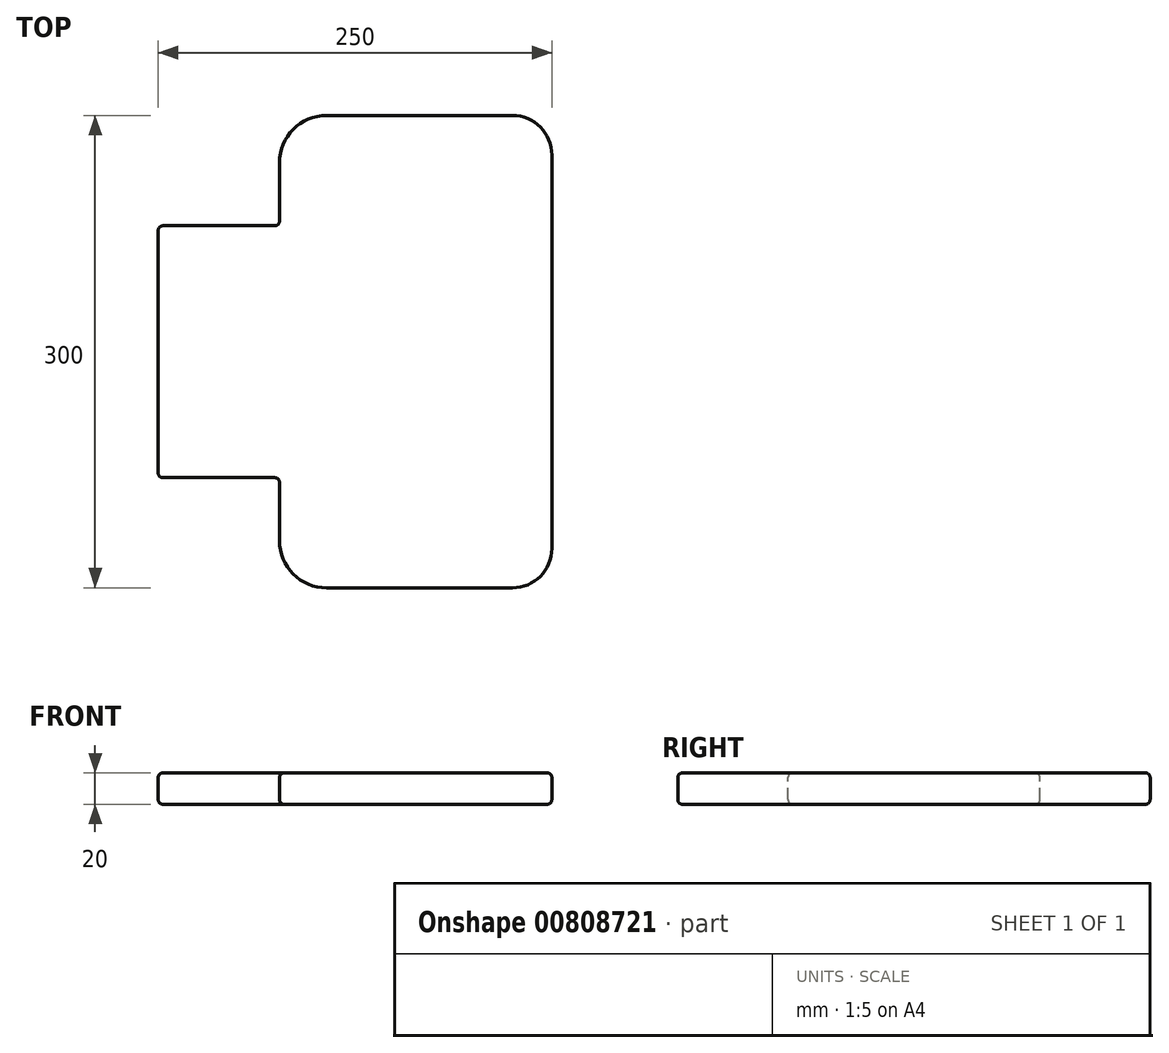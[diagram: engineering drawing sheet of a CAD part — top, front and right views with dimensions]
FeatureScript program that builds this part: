
annotation { "Feature Type Name" : "Feature", "Feature Type Description" : "" }
export const myFeature = defineFeature(function(context is Context, id is Id, definition is map)
    precondition{}
    {
        {
            var Q0;
            Q0=qCreatedBy(makeId("Top.planeOp"),FACE);
            var sketch = newSketch(context, id + "F0", { "sketchPlane" : qUnion([Q0])});
            skLineSegment(sketch, "E0.bottom", {"start": v(100, -150) * mm, "end": v(-100, -150) * mm});
            skLineSegment(sketch, "E0.top", {"start": v(100, 150) * mm, "end": v(-100, 150) * mm});
            skLineSegment(sketch, "E0.left", {"start": v(125, -125) * mm, "end": v(125, 125) * mm});
            skLineSegment(sketch, "E0.right", {"start": v(-125, -125) * mm, "end": v(-125, 125) * mm});
            skPoint(sketch, "E0.middle", {"position": v(0, 0) * mm});
            skPoint(sketch, "E1.visualSharp", {"position": v(-125, 150) * mm});
            skArc(sketch, "E1.filletArc", {"start": v(-100, 150) * mm, "mid": v(-117.68, 142.68) * mm, "end": v(-125, 125) * mm});
            skPoint(sketch, "E2.visualSharp", {"position": v(125, 150) * mm});
            skArc(sketch, "E2.filletArc", {"start": v(125, 125) * mm, "mid": v(117.68, 142.68) * mm, "end": v(100, 150) * mm});
            skPoint(sketch, "E3.visualSharp", {"position": v(125, -150) * mm});
            skArc(sketch, "E3.filletArc", {"start": v(100, -150) * mm, "mid": v(117.68, -142.68) * mm, "end": v(125, -125) * mm});
            skPoint(sketch, "E4.visualSharp", {"position": v(-125, -150) * mm});
            skArc(sketch, "E4.filletArc", {"start": v(-125, -125) * mm, "mid": v(-117.68, -142.68) * mm, "end": v(-100, -150) * mm});
            skSolve(sketch);
        }
        {
            var Q0;
            Q0=makeQuery(id+"F0.imprint","IMPRINT",FACE,{"disambiguationData":[TD([[makeQuery(id+"F0.imprint","IMPRINT",EDGE,{"derivedFrom":sQuery(id+"F0.wireOp",EDGE,"E0.bottom")}),-1.0]])]});
            extrude(context, id + "F1", {"entities" : qUnion([Q0]), "depth" : 20 * mm, "offsetDistance" : 25 * mm});
        }
        {
            var Q0;
            Q0=makeQuery(id+"F1.opExtrude","CAP_FACE",FACE,{"disambiguationData":[OSD([sQuery(id+"F0.wireOp",EDGE,"E0.bottom"),sQuery(id+"F0.wireOp",EDGE,"E0.top"),sQuery(id+"F0.wireOp",EDGE,"E0.left"),sQuery(id+"F0.wireOp",EDGE,"E0.right"),sQuery(id+"F0.wireOp",EDGE,"E1.filletArc"),sQuery(id+"F0.wireOp",EDGE,"E2.filletArc"),sQuery(id+"F0.wireOp",EDGE,"E3.filletArc"),sQuery(id+"F0.wireOp",EDGE,"E4.filletArc")])],"isStart":false});
            var sketch = newSketch(context, id + "F2", { "sketchPlane" : qUnion([Q0])});
            skLineSegment(sketch, "E5.bottom", {"start": v(-146.1, -80) * mm, "end": v(-48, -80) * mm});
            skLineSegment(sketch, "E5.top", {"start": v(-146.1, -176.23) * mm, "end": v(-48, -176.23) * mm});
            skLineSegment(sketch, "E5.left", {"start": v(-146.1, -80) * mm, "end": v(-146.1, -176.23) * mm});
            skLineSegment(sketch, "E5.right", {"start": v(-48, -80) * mm, "end": v(-48, -176.23) * mm});
            skLineSegment(sketch, "E6.MirrorCS", {"start": v(-146.1, 80) * mm, "end": v(-48, 80) * mm});
            skLineSegment(sketch, "E7.MirrorCS", {"start": v(-48, 80) * mm, "end": v(-48, 176.23) * mm});
            skLineSegment(sketch, "E8.MirrorCS", {"start": v(-146.1, 80) * mm, "end": v(-146.1, 176.23) * mm});
            skLineSegment(sketch, "E9.MirrorCS", {"start": v(-146.1, 176.23) * mm, "end": v(-48, 176.23) * mm});
            skSolve(sketch);
        }
        {
            var Q0;
            {var subQ0=makeQuery(id+"F1.opExtrude","CAP_EDGE",EDGE,{"disambiguationData":[OSD([sQuery(id+"F0.wireOp",EDGE,"E4.filletArc")])],"isStart":false});Q0=makeQuery(id+"F2.imprint","IMPRINT",FACE,{"disambiguationData":[TD([[makeQuery(id+"F2.imprint","IMPRINT",EDGE,{"derivedFrom":subQ0}),1.0]])]});}
            var Q1;
            {var subQ1=sQuery(id+"F2.wireOp",EDGE,"E5.top");Q1=makeQuery(id+"F2.imprint","IMPRINT",FACE,{"disambiguationData":[TD([[makeQuery(id+"F2.imprint","IMPRINT",EDGE,{"derivedFrom":subQ1}),1.0]])]});}
            var Q2;
            {var subQ0=sQuery(id+"F2.wireOp",EDGE,"E8.MirrorCS");Q2=makeQuery(id+"F2.imprint","IMPRINT",FACE,{"disambiguationData":[TD([[makeQuery(id+"F2.imprint","IMPRINT",EDGE,{"derivedFrom":subQ0}),-1.0]])]});}
            var Q3;
            {var subQ0=makeQuery(id+"F1.opExtrude","CAP_EDGE",EDGE,{"disambiguationData":[OSD([sQuery(id+"F0.wireOp",EDGE,"E1.filletArc")])],"isStart":false});Q3=makeQuery(id+"F2.imprint","IMPRINT",FACE,{"disambiguationData":[TD([[makeQuery(id+"F2.imprint","IMPRINT",EDGE,{"derivedFrom":subQ0}),1.0]])]});}
            extrude(context, id + "F3", {"entities" : qUnion([Q0, Q1, Q2, Q3]), "operationType" : NewBodyOperationType.REMOVE, "oppositeDirection" : true, "depth" : 25 * mm, "offsetDistance" : 25 * mm});
        }
        {
            var Q0;
            Q0=makeQuery(id+"F3.boolean.opBoolean","INTERSECT",EDGE,{"derivedFrom":[makeQuery(id+"F1.opExtrude","SWEPT_FACE",FACE,{"disambiguationData":[OSD([sQuery(id+"F0.wireOp",EDGE,"E0.bottom")])]}),makeQuery(id+"F3.opExtrude","SWEPT_FACE",FACE,{"disambiguationData":[OSD([sQuery(id+"F2.wireOp",EDGE,"E5.right")])]})]});
            var Q1;
            Q1=makeQuery(id+"F3.boolean.opBoolean","INTERSECT",EDGE,{"derivedFrom":[makeQuery(id+"F1.opExtrude","SWEPT_FACE",FACE,{"disambiguationData":[OSD([sQuery(id+"F0.wireOp",EDGE,"E0.top")])]}),makeQuery(id+"F3.opExtrude","SWEPT_FACE",FACE,{"disambiguationData":[OSD([sQuery(id+"F2.wireOp",EDGE,"E7.MirrorCS")])]})]});
            fillet(context, id + "F4", {"entities" : qUnion([Q0, Q1]), "radius" : 30 * mm, "tangentPropagation" : true, "allowEdgeOverflow" : false});
        }
        {
            var Q0;
            Q0=makeQuery(id+"F3.boolean.opBoolean","COPY",EDGE,{"derivedFrom":makeQuery(id+"F3.opExtrude","SWEPT_EDGE",EDGE,{"disambiguationData":[OSD([sQuery(id+"F2.wireOp",EDGE,"E6.MirrorCS"),sQuery(id+"F2.wireOp",EDGE,"E7.MirrorCS")])]})});
            var Q1;
            Q1=makeQuery(id+"F3.boolean.opBoolean","INTERSECT",EDGE,{"derivedFrom":[makeQuery(id+"F1.opExtrude","SWEPT_FACE",FACE,{"disambiguationData":[OSD([sQuery(id+"F0.wireOp",EDGE,"E0.right")])]}),makeQuery(id+"F3.opExtrude","SWEPT_FACE",FACE,{"disambiguationData":[OSD([sQuery(id+"F2.wireOp",EDGE,"E6.MirrorCS")])]})]});
            var Q2;
            Q2=makeQuery(id+"F3.boolean.opBoolean","COPY",EDGE,{"derivedFrom":makeQuery(id+"F3.opExtrude","SWEPT_EDGE",EDGE,{"disambiguationData":[OSD([sQuery(id+"F2.wireOp",EDGE,"E5.bottom"),sQuery(id+"F2.wireOp",EDGE,"E5.right")])]})});
            var Q3;
            Q3=makeQuery(id+"F3.boolean.opBoolean","INTERSECT",EDGE,{"derivedFrom":[makeQuery(id+"F1.opExtrude","SWEPT_FACE",FACE,{"disambiguationData":[OSD([sQuery(id+"F0.wireOp",EDGE,"E0.right")])]}),makeQuery(id+"F3.opExtrude","SWEPT_FACE",FACE,{"disambiguationData":[OSD([sQuery(id+"F2.wireOp",EDGE,"E5.bottom")])]})]});
            fillet(context, id + "F5", {"entities" : qUnion([Q0, Q1, Q2, Q3]), "radius" : 3 * mm, "tangentPropagation" : true, "allowEdgeOverflow" : false});
        }
        {
            var Q0;
            Q0=makeQuery(id+"F1.opExtrude","CAP_FACE",FACE,{"disambiguationData":[OSD([sQuery(id+"F0.wireOp",EDGE,"E0.bottom"),sQuery(id+"F0.wireOp",EDGE,"E0.top"),sQuery(id+"F0.wireOp",EDGE,"E0.left"),sQuery(id+"F0.wireOp",EDGE,"E0.right"),sQuery(id+"F0.wireOp",EDGE,"E1.filletArc"),sQuery(id+"F0.wireOp",EDGE,"E2.filletArc"),sQuery(id+"F0.wireOp",EDGE,"E3.filletArc"),sQuery(id+"F0.wireOp",EDGE,"E4.filletArc")])],"isStart":false});
            var Q1;
            Q1=makeQuery(id+"F1.opExtrude","CAP_FACE",FACE,{"disambiguationData":[OSD([sQuery(id+"F0.wireOp",EDGE,"E0.bottom"),sQuery(id+"F0.wireOp",EDGE,"E0.top"),sQuery(id+"F0.wireOp",EDGE,"E0.left"),sQuery(id+"F0.wireOp",EDGE,"E0.right"),sQuery(id+"F0.wireOp",EDGE,"E1.filletArc"),sQuery(id+"F0.wireOp",EDGE,"E2.filletArc"),sQuery(id+"F0.wireOp",EDGE,"E3.filletArc"),sQuery(id+"F0.wireOp",EDGE,"E4.filletArc")])],"isStart":true});
            fillet(context, id + "F6", {"entities" : qUnion([Q0, Q1]), "radius" : 3 * mm, "tangentPropagation" : true, "allowEdgeOverflow" : false});
        }
        {
            var Q0;
            Q0=makeQuery(id+"F3.boolean.opBoolean","COPY",FACE,{"derivedFrom":makeQuery(id+"F3.opExtrude","SWEPT_FACE",FACE,{"disambiguationData":[OSD([sQuery(id+"F2.wireOp",EDGE,"E5.right")])]})});
            var sketch = newSketch(context, id + "F7", { "sketchPlane" : qUnion([Q0])});
            skLineSegment(sketch, "E10.0", {"start": v(80, 3) * mm, "end": v(80, 17) * mm});
            skLineSegment(sketch, "E11", {"start": v(120, 10) * mm, "end": v(89, 10) * mm});
            skPoint(sketch, "E12", {"position": v(89, 10) * mm});
            skSolve(sketch);
        }
        {
            var Q0;
            Q0=makeQuery(id+"F3.boolean.opBoolean","COPY",FACE,{"derivedFrom":makeQuery(id+"F3.opExtrude","SWEPT_FACE",FACE,{"disambiguationData":[OSD([sQuery(id+"F2.wireOp",EDGE,"E7.MirrorCS")])]})});
            var sketch = newSketch(context, id + "F8", { "sketchPlane" : qUnion([Q0])});
            skPoint(sketch, "E13.0", {"position": v(-80, 10) * mm});
            skLineSegment(sketch, "E14.0", {"start": v(-80, 17) * mm, "end": v(-80, 3) * mm});
            skLineSegment(sketch, "E15", {"start": v(-80, 10) * mm, "end": v(-89, 10) * mm});
            skPoint(sketch, "E16", {"position": v(-89, 10) * mm});
            skSolve(sketch);
        }
    });
